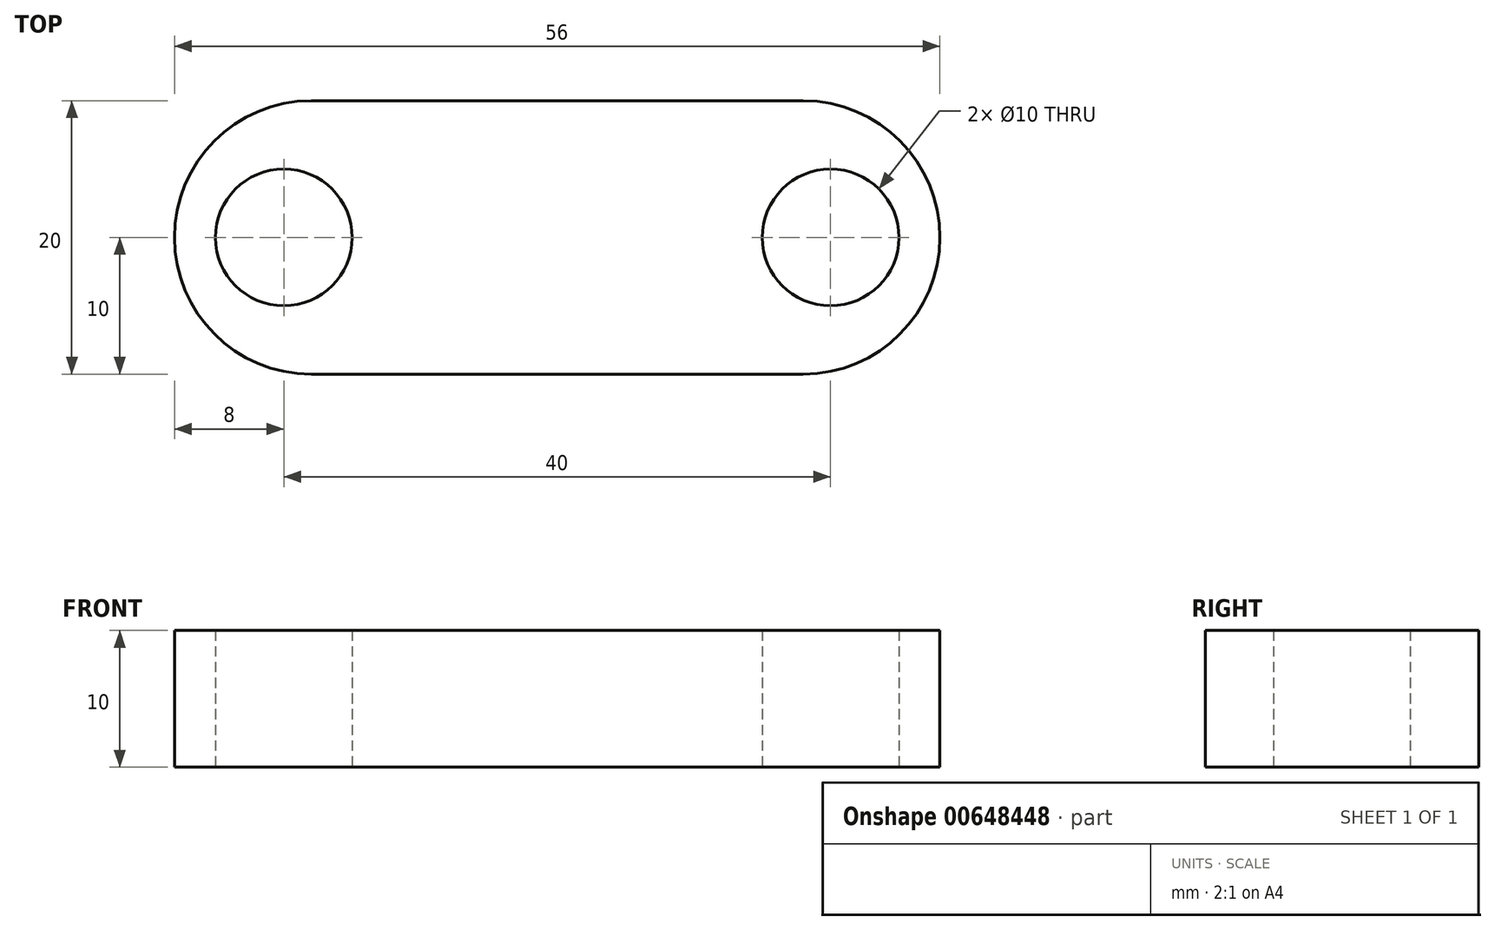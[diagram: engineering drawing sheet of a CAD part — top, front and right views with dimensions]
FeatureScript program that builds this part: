
annotation { "Feature Type Name" : "Feature", "Feature Type Description" : "" }
export const myFeature = defineFeature(function(context is Context, id is Id, definition is map)
    precondition{}
    {
        {
            var Q0;
            Q0=qCreatedBy(makeId("Top.planeOp"),FACE);
            var sketch = newSketch(context, id + "F0", { "sketchPlane" : qUnion([Q0])});
            skLineSegment(sketch, "E0.bottom", {"start": v(28, 10) * mm, "end": v(-28, 10) * mm});
            skLineSegment(sketch, "E0.top", {"start": v(28, -10) * mm, "end": v(-28, -10) * mm});
            skLineSegment(sketch, "E0.left", {"start": v(28, 10) * mm, "end": v(28, -10) * mm});
            skLineSegment(sketch, "E0.right", {"start": v(-28, 10) * mm, "end": v(-28, -10) * mm});
            skPoint(sketch, "E0.middle", {"position": v(0, 0) * mm});
            skCircle(sketch, "E1", {"center": v(-20, 0) * mm, "radius": 5 * mm});
            skCircle(sketch, "E2", {"center": v(20, 0) * mm, "radius": 5 * mm});
            skSolve(sketch);
        }
        {
            var Q0;
            Q0 = qSketchRegion(id + "F0", true);
            extrude(context, id + "F1", {"entities" : qUnion([Q0]), "depth" : 10 * mm, "offsetDistance" : 25 * mm});
        }
        {
            var Q0;
            Q0=makeQuery(id+"F1.opExtrude","SWEPT_EDGE",EDGE,{"disambiguationData":[OSD([sQuery(id+"F0.wireOp",EDGE,"E0.bottom"),sQuery(id+"F0.wireOp",EDGE,"E0.right")])]});
            var Q1;
            Q1=makeQuery(id+"F1.opExtrude","SWEPT_EDGE",EDGE,{"disambiguationData":[OSD([sQuery(id+"F0.wireOp",EDGE,"E0.top"),sQuery(id+"F0.wireOp",EDGE,"E0.right")])]});
            var Q2;
            Q2=makeQuery(id+"F1.opExtrude","SWEPT_EDGE",EDGE,{"disambiguationData":[OSD([sQuery(id+"F0.wireOp",EDGE,"E0.bottom"),sQuery(id+"F0.wireOp",EDGE,"E0.left")])]});
            var Q3;
            Q3=makeQuery(id+"F1.opExtrude","SWEPT_EDGE",EDGE,{"disambiguationData":[OSD([sQuery(id+"F0.wireOp",EDGE,"E0.top"),sQuery(id+"F0.wireOp",EDGE,"E0.left")])]});
            fillet(context, id + "F2", {"entities" : qUnion([Q0, Q1, Q2, Q3]), "radius" : 10 * mm, "tangentPropagation" : true, "allowEdgeOverflow" : false});
        }
    });
